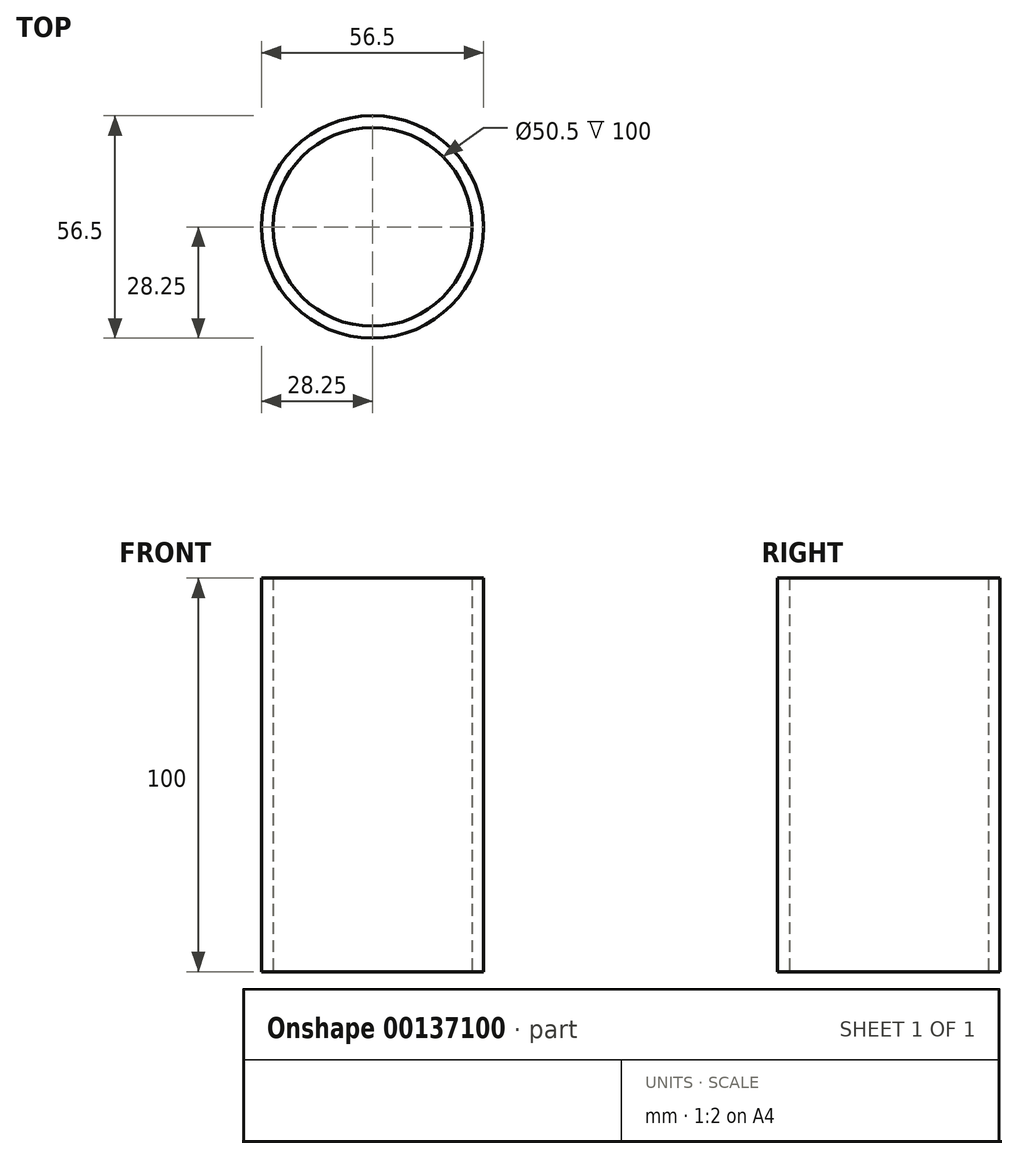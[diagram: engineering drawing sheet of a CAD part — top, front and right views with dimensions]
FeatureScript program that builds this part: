
annotation { "Feature Type Name" : "Feature", "Feature Type Description" : "" }
export const myFeature = defineFeature(function(context is Context, id is Id, definition is map)
    precondition{}
    {
        {
            var Q0;
            Q0=qCreatedBy(makeId("Top.planeOp"),FACE);
            var sketch = newSketch(context, id + "F0", { "sketchPlane" : qUnion([Q0])});
            skCircle(sketch, "E0", {"center": v(0, 0) * mm, "radius": 25.25 * mm});
            skCircle(sketch, "E1", {"center": v(0, 0) * mm, "radius": 28.25 * mm});
            skSolve(sketch);
        }
        {
            var Q0;
            Q0=makeQuery(id+"F0.imprint","IMPRINT",FACE,{"disambiguationData":[TD([[makeQuery(id+"F0.imprint","IMPRINT",EDGE,{"derivedFrom":sQuery(id+"F0.wireOp",EDGE,"E0")}),-1.0]])]});
            extrude(context, id + "F1", {"entities" : qUnion([Q0]), "endBound" : BoundingType.SYMMETRIC, "depth" : 100 * mm});
        }
    });
